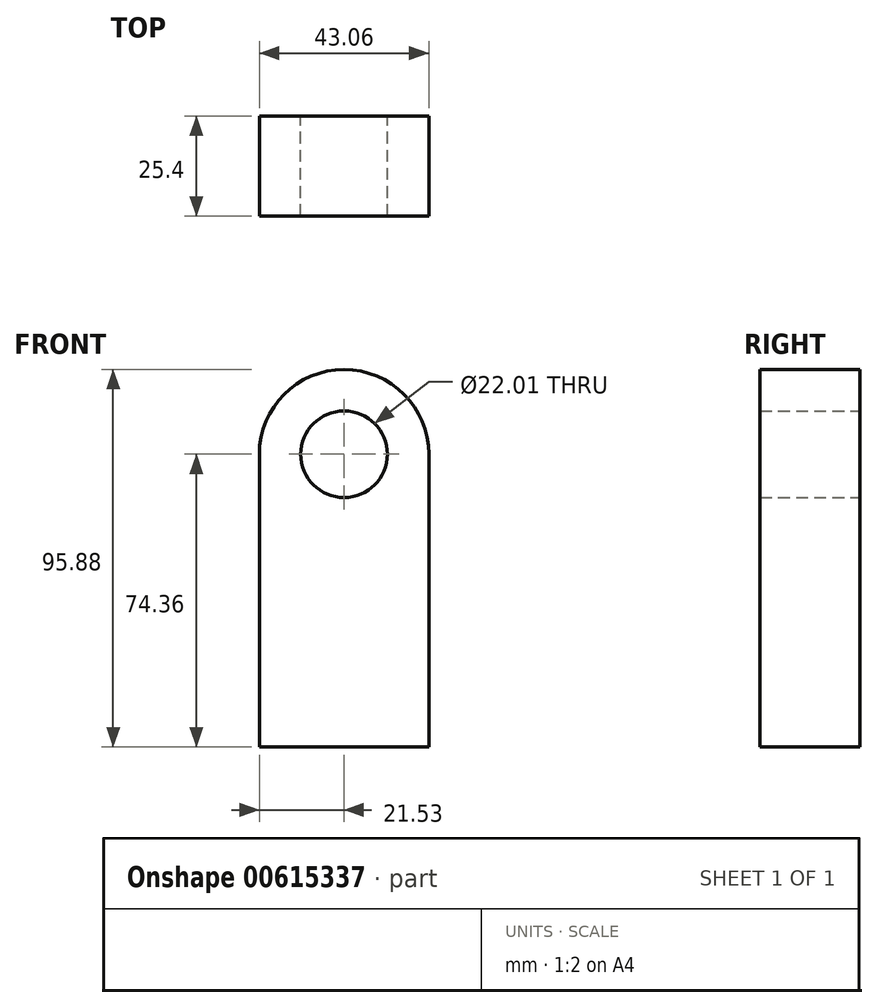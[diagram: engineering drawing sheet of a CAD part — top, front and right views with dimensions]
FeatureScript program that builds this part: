
annotation { "Feature Type Name" : "Feature", "Feature Type Description" : "" }
export const myFeature = defineFeature(function(context is Context, id is Id, definition is map)
    precondition{}
    {
        {
            var Q0;
            Q0=qCreatedBy(makeId("Front.planeOp"),FACE);
            var sketch = newSketch(context, id + "F0", { "sketchPlane" : qUnion([Q0])});
            skLineSegment(sketch, "E0.top", {"start": v(-21.53, -37.18) * mm, "end": v(21.53, -37.18) * mm});
            skLineSegment(sketch, "E0.left", {"start": v(-21.53, 37.18) * mm, "end": v(-21.53, -37.18) * mm});
            skLineSegment(sketch, "E0.right", {"start": v(21.53, 37.18) * mm, "end": v(21.53, -37.18) * mm});
            skPoint(sketch, "E0.middle", {"position": v(0, 0) * mm});
            skArc(sketch, "E1", {"start": v(21.53, 37.18) * mm, "mid": v(0, 58.7) * mm, "end": v(-21.53, 37.18) * mm});
            skCircle(sketch, "E2", {"center": v(0, 37.18) * mm, "radius": 11 * mm});
            skSolve(sketch);
        }
        {
            var Q0;
            Q0 = qSketchRegion(id + "F0", true);
            extrude(context, id + "F1", {"entities" : qUnion([Q0]), "depth" : 25.4 * mm, "offsetDistance" : 25.4 * mm});
        }
    });
